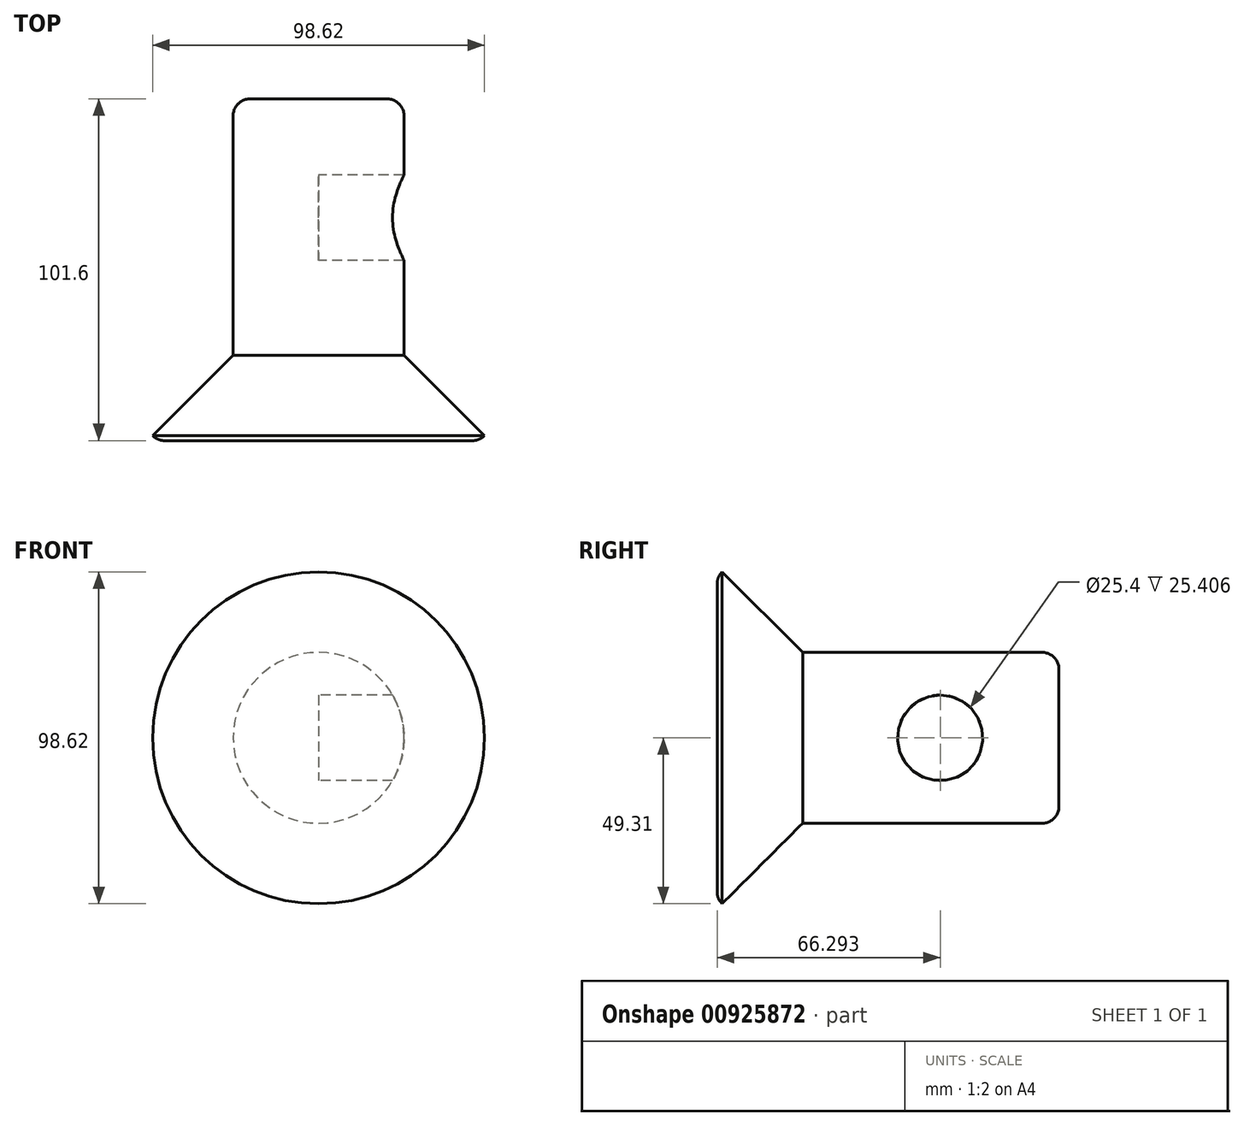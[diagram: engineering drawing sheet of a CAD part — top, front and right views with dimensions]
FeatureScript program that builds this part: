
annotation { "Feature Type Name" : "Feature", "Feature Type Description" : "" }
export const myFeature = defineFeature(function(context is Context, id is Id, definition is map)
    precondition{}
    {
        {
            var Q0;
            Q0=qCreatedBy(makeId("Front.planeOp"),FACE);
            var sketch = newSketch(context, id + "F0", { "sketchPlane" : qUnion([Q0])});
            skCircle(sketch, "E0", {"center": v(0, 0) * mm, "radius": 50.8 * mm});
            skSolve(sketch);
        }
        {
            var Q0;
            Q0=makeQuery(id+"F0.imprint","IMPRINT",FACE,{"disambiguationData":[TD([[makeQuery(id+"F0.imprint","IMPRINT",EDGE,{"derivedFrom":sQuery(id+"F0.wireOp",EDGE,"E0")}),1.0]])]});
            extrude(context, id + "F1", {"entities" : qUnion([Q0]), "depth" : 25.4 * mm, "offsetDistance" : 25.4 * mm});
        }
        {
            var Q0;
            Q0=makeQuery(id+"F1.opExtrude","CAP_EDGE",EDGE,{"disambiguationData":[OSD([sQuery(id+"F0.wireOp",EDGE,"E0")])],"isStart":false});
            fillet(context, id + "F2", {"entities" : qUnion([Q0]), "radius" : 5.08 * mm, "tangentPropagation" : true, "allowEdgeOverflow" : false});
        }
        {
            var Q0;
            Q0=makeQuery(id+"F1.opExtrude","CAP_EDGE",EDGE,{"disambiguationData":[OSD([sQuery(id+"F0.wireOp",EDGE,"E0")])],"isStart":true});
            chamfer(context, id + "F3", {"entities" : qUnion([Q0]), "width" : 25.4 * mm, "tangentPropagation" : true});
        }
        {
            var Q0;
            Q0=makeQuery(id+"F1.opExtrude","CAP_FACE",FACE,{"disambiguationData":[OSD([sQuery(id+"F0.wireOp",EDGE,"E0")])],"isStart":true});
            extrude(context, id + "F4", {"entities" : qUnion([Q0]), "depth" : 76.2 * mm, "offsetDistance" : 25.4 * mm});
        }
        {
            var Q0;
            Q0=makeQuery(id+"F4.opExtrude","CAP_EDGE",EDGE,{"disambiguationData":[OSD([sQuery(id+"F0.wireOp",EDGE,"E0")])],"isStart":false});
            fillet(context, id + "F5", {"entities" : qUnion([Q0]), "radius" : 5.08 * mm, "tangentPropagation" : true, "allowEdgeOverflow" : false});
        }
        {
            var Q0;
            Q0=qCreatedBy(makeId("Right.planeOp"),FACE);
            var sketch = newSketch(context, id + "F6", { "sketchPlane" : qUnion([Q0])});
            skCircle(sketch, "E1", {"center": v(40.9, 0) * mm, "radius": 12.7 * mm});
            skSolve(sketch);
        }
        {
            var Q0;
            Q0=sQuery(id+"F6.wireOp",VERTEX,"E1.center");
            var Q1;
            Q1=makeQuery(id+"F4.opExtrude","SWEPT_BODY",BODY,{"disambiguationData":[OSD([sQuery(id+"F0.wireOp",EDGE,"E0")])]});
            hole(context, id + "F7", {"style" : HoleStyle.SIMPLE, "endStyle" : HoleEndStyle.THROUGH, "oppositeDirection" : true, "holeDiameter" : 25.4 * mm, "majorDiameter" : 6.35 * mm, "isTappedThrough" : true, "tappedDepth" : 12.7 * mm, "tapClearance" : 3, "locations" : qUnion([Q0]), "scope" : qUnion([Q1])});
        }
    });
